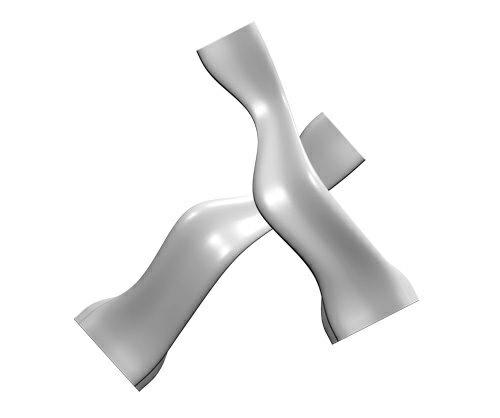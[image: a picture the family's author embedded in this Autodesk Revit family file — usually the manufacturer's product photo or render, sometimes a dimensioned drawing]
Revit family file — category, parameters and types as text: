
# Revit family: CITY ALPHABET litera „X”
name_source: partatom
category: Meble
revit_build: Autodesk Revit 2018 (Build: 20190510_1515(x64)
units: mm (PartAtom-declared; Revit-internal decimal feet)

## family parameters
Numer OmniClass = 23.40.10.11.14
Obiekt nadrzędny = Powierzchnia
Punkt obliczania pomieszczeń = Nie
Tnij formami wycięć po wczytaniu = Nie
Tytuł OmniClass = Exterior Seating
Współdzielony = Nie

## types (1)
- CITY ALPHABET litera „X”
    Domyślna rzędna = 1219 mm
    Długość = 2750 mm  [stored 9.02231 ft]
    IfcExportAs = IfcFurnishingElement
    Komentarze do typu = Ławka
    Materiał - informacja = Szeroki wybór kolorów wg palety RAL. Istnieje również możliwość specjalnego wykonania kolorystycznego na indywidualne zapytanie klienta.
    Model = CITY ALPHABET litera „X”
    Obraz typu = X.jpg
    Producent = Astrini Design
    Szerokość = 2550 mm  [stored 8.36614 ft]
    Temepratura użytkowania = -40°C do 80°C, ( -40°F do 176°F )
    URL = http://astrini-design.pl
    Waga (szacunkowo) = 69.00 kg
    Waga po wypełnieniu (szacunkowo) = 169.00 kg
    Wysokość = 590 mm  [stored 1.9357 ft]

note: [stored X ft] marks values corroborated as IEEE doubles in the binary element streams (Revit-internal decimal feet)
